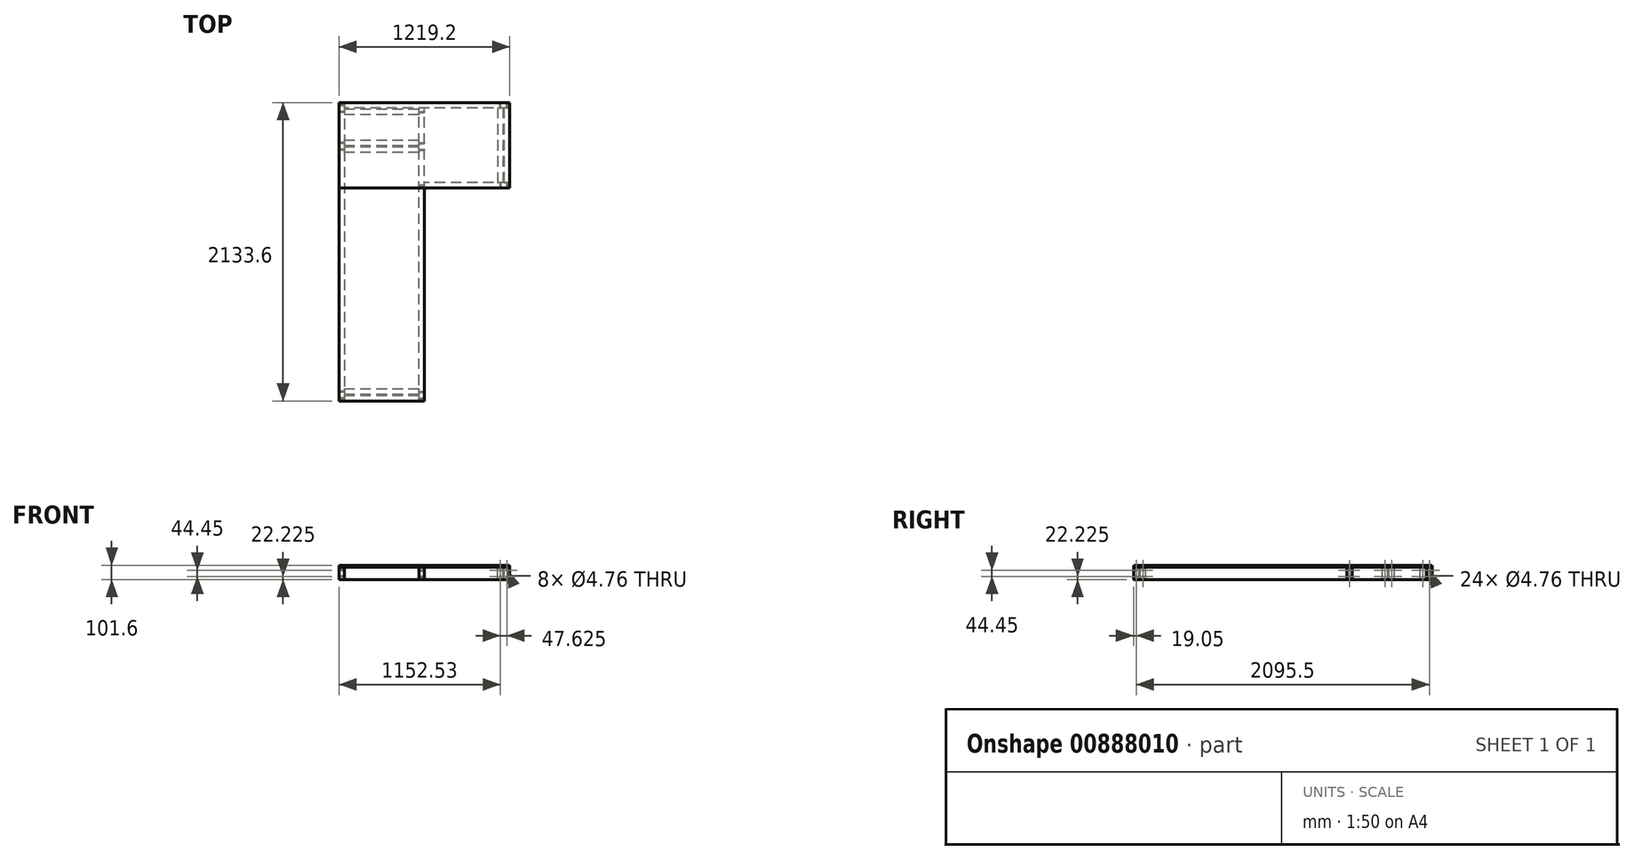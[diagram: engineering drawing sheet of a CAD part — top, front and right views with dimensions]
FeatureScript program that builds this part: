
annotation { "Feature Type Name" : "Feature", "Feature Type Description" : "" }
export const myFeature = defineFeature(function(context is Context, id is Id, definition is map)
    precondition{}
    {
        {
            var Q0;
            Q0=qCreatedBy(makeId("Top.planeOp"),FACE);
            var sketch = newSketch(context, id + "F0", { "sketchPlane" : qUnion([Q0])});
            skLineSegment(sketch, "E0.bottom", {"start": v(0, 0) * mm, "end": v(1219.2, 0) * mm});
            skLineSegment(sketch, "E0.top", {"start": v(0, 609.6) * mm, "end": v(1219.2, 609.6) * mm});
            skLineSegment(sketch, "E0.left", {"start": v(0, 0) * mm, "end": v(0, 609.6) * mm});
            skLineSegment(sketch, "E0.right", {"start": v(1219.2, 0) * mm, "end": v(1219.2, 609.6) * mm});
            skLineSegment(sketch, "E1.bottom", {"start": v(0, 0) * mm, "end": v(609.6, 0) * mm});
            skSolve(sketch);
        }
        {
            var Q0;
            Q0 = qSketchRegion(id + "F0", true);
            extrude(context, id + "F1", {"entities" : qUnion([Q0]), "depth" : 12.7 * mm, "offsetDistance" : 25.4 * mm});
        }
        {
            var Q0;
            Q0=qCreatedBy(makeId("Top.planeOp"),FACE);
            var sketch = newSketch(context, id + "F2", { "sketchPlane" : qUnion([Q0])});
            skLineSegment(sketch, "E2.bottom", {"start": v(0, 0) * mm, "end": v(609.6, 0) * mm});
            skLineSegment(sketch, "E2.top", {"start": v(0, -1524) * mm, "end": v(609.6, -1524) * mm});
            skLineSegment(sketch, "E2.left", {"start": v(0, 0) * mm, "end": v(0, -1524) * mm});
            skLineSegment(sketch, "E2.right", {"start": v(609.6, 0) * mm, "end": v(609.6, -1524) * mm});
            skSolve(sketch);
        }
        {
            var Q0;
            Q0 = qSketchRegion(id + "F2", true);
            extrude(context, id + "F3", {"entities" : qUnion([Q0]), "depth" : 12.7 * mm, "offsetDistance" : 25.4 * mm});
        }
        {
            var Q0;
            Q0=qCreatedBy(makeId("Top.planeOp"),FACE);
            var sketch = newSketch(context, id + "F4", { "sketchPlane" : qUnion([Q0])});
            skLineSegment(sketch, "E3.bottom", {"start": v(38.1, 609.6) * mm, "end": v(0, 609.6) * mm});
            skLineSegment(sketch, "E3.top", {"start": v(38.1, -1524) * mm, "end": v(0, -1524) * mm});
            skLineSegment(sketch, "E3.left", {"start": v(38.1, 609.6) * mm, "end": v(38.1, -1524) * mm});
            skLineSegment(sketch, "E3.right", {"start": v(0, 609.6) * mm, "end": v(0, -1524) * mm});
            skPoint(sketch, "E4", {"position": v(0, 0) * mm});
            skLineSegment(sketch, "E5.bottom", {"start": v(609.6, -1524) * mm, "end": v(571.5, -1524) * mm});
            skLineSegment(sketch, "E5.top", {"start": v(609.6, 571.5) * mm, "end": v(571.5, 571.5) * mm});
            skLineSegment(sketch, "E5.left", {"start": v(609.6, -1524) * mm, "end": v(609.6, 571.5) * mm});
            skLineSegment(sketch, "E5.right", {"start": v(571.5, -1524) * mm, "end": v(571.5, 571.5) * mm});
            skLineSegment(sketch, "E6.bottom", {"start": v(1219.2, 609.6) * mm, "end": v(38.1, 609.6) * mm});
            skLineSegment(sketch, "E6.top", {"start": v(1219.2, 571.5) * mm, "end": v(38.1, 571.5) * mm});
            skLineSegment(sketch, "E6.left", {"start": v(1219.2, 609.6) * mm, "end": v(1219.2, 571.5) * mm});
            skLineSegment(sketch, "E6.right", {"start": v(38.1, 609.6) * mm, "end": v(38.1, 571.5) * mm});
            skLineSegment(sketch, "E7.bottom", {"start": v(1219.2, 0) * mm, "end": v(609.6, 0) * mm});
            skLineSegment(sketch, "E7.top", {"start": v(1219.2, 38.1) * mm, "end": v(609.6, 38.1) * mm});
            skLineSegment(sketch, "E7.left", {"start": v(1219.2, 0) * mm, "end": v(1219.2, 38.1) * mm});
            skLineSegment(sketch, "E7.right", {"start": v(609.6, 0) * mm, "end": v(609.6, 38.1) * mm});
            skLineSegment(sketch, "E8.bottom", {"start": v(1219.2, 38.1) * mm, "end": v(1181.1, 38.1) * mm});
            skLineSegment(sketch, "E8.top", {"start": v(1219.2, 571.5) * mm, "end": v(1181.1, 571.5) * mm});
            skLineSegment(sketch, "E8.left", {"start": v(1219.2, 38.1) * mm, "end": v(1219.2, 571.5) * mm});
            skLineSegment(sketch, "E8.right", {"start": v(1181.1, 38.1) * mm, "end": v(1181.1, 571.5) * mm});
            skLineSegment(sketch, "E9.bottom", {"start": v(571.5, -1524) * mm, "end": v(38.1, -1524) * mm});
            skLineSegment(sketch, "E9.top", {"start": v(571.5, -1485.9) * mm, "end": v(38.1, -1485.9) * mm});
            skLineSegment(sketch, "E9.left", {"start": v(571.5, -1524) * mm, "end": v(571.5, -1485.9) * mm});
            skLineSegment(sketch, "E9.right", {"start": v(38.1, -1524) * mm, "end": v(38.1, -1485.9) * mm});
            skLineSegment(sketch, "E10.bottom", {"start": v(571.5, 254) * mm, "end": v(38.1, 254) * mm});
            skLineSegment(sketch, "E10.top", {"start": v(571.5, 292.1) * mm, "end": v(38.1, 292.1) * mm});
            skLineSegment(sketch, "E10.left", {"start": v(571.5, 254) * mm, "end": v(571.5, 292.1) * mm});
            skLineSegment(sketch, "E10.right", {"start": v(38.1, 254) * mm, "end": v(38.1, 292.1) * mm});
            skLineSegment(sketch, "E11.bottom", {"start": v(571.5, 301.63) * mm, "end": v(38.1, 301.63) * mm});
            skLineSegment(sketch, "E11.top", {"start": v(571.5, 339.73) * mm, "end": v(38.1, 339.73) * mm});
            skLineSegment(sketch, "E11.left", {"start": v(571.5, 301.63) * mm, "end": v(571.5, 339.72) * mm});
            skLineSegment(sketch, "E11.right", {"start": v(38.1, 301.62) * mm, "end": v(38.1, 339.73) * mm});
            skLineSegment(sketch, "E12.bottom", {"start": v(571.5, -1476.38) * mm, "end": v(38.1, -1476.38) * mm});
            skLineSegment(sketch, "E12.top", {"start": v(571.5, -1438.28) * mm, "end": v(38.1, -1438.28) * mm});
            skLineSegment(sketch, "E12.left", {"start": v(571.5, -1476.38) * mm, "end": v(571.5, -1438.28) * mm});
            skLineSegment(sketch, "E12.right", {"start": v(38.1, -1476.38) * mm, "end": v(38.1, -1438.28) * mm});
            skLineSegment(sketch, "E13.bottom", {"start": v(571.5, 561.98) * mm, "end": v(38.1, 561.98) * mm});
            skLineSegment(sketch, "E13.top", {"start": v(571.5, 523.88) * mm, "end": v(38.1, 523.88) * mm});
            skLineSegment(sketch, "E13.left", {"start": v(571.5, 561.98) * mm, "end": v(571.5, 523.88) * mm});
            skLineSegment(sketch, "E13.right", {"start": v(38.1, 561.98) * mm, "end": v(38.1, 523.88) * mm});
            skLineSegment(sketch, "E14.bottom", {"start": v(1171.58, 571.5) * mm, "end": v(1133.47, 571.5) * mm});
            skLineSegment(sketch, "E14.top", {"start": v(1171.58, 38.1) * mm, "end": v(1133.48, 38.1) * mm});
            skLineSegment(sketch, "E14.left", {"start": v(1171.58, 571.5) * mm, "end": v(1171.58, 38.1) * mm});
            skLineSegment(sketch, "E14.right", {"start": v(1133.47, 571.5) * mm, "end": v(1133.47, 38.1) * mm});
            skLineSegment(sketch, "E15", {"start": v(38.1, 320.68) * mm, "end": v(571.5, 320.68) * mm, "construction": true});
            skLineSegment(sketch, "E16", {"start": v(38.1, 273.05) * mm, "end": v(571.5, 273.05) * mm, "construction": true});
            skLineSegment(sketch, "E17", {"start": v(38.1, 542.93) * mm, "end": v(571.5, 542.93) * mm, "construction": true});
            skLineSegment(sketch, "E18", {"start": v(38.1, 590.55) * mm, "end": v(1219.2, 590.55) * mm, "construction": true});
            skLineSegment(sketch, "E19", {"start": v(1152.53, 571.5) * mm, "end": v(1152.53, 38.1) * mm, "construction": true});
            skLineSegment(sketch, "E20", {"start": v(1200.15, 38.1) * mm, "end": v(1200.15, 571.5) * mm, "construction": true});
            skLineSegment(sketch, "E21", {"start": v(38.1, -1457.33) * mm, "end": v(571.5, -1457.33) * mm, "construction": true});
            skLineSegment(sketch, "E22", {"start": v(38.1, -1504.95) * mm, "end": v(571.5, -1504.95) * mm, "construction": true});
            skSolve(sketch);
        }
        {
            var Q0;
            {var subQ1=sQuery(id+"F4.wireOp",EDGE,"E3.bottom");Q0=makeQuery(id+"F4.imprint","IMPRINT",FACE,{"disambiguationData":[TD([[makeQuery(id+"F4.imprint","IMPRINT",EDGE,{"derivedFrom":subQ1}),1.0]])]});}
            extrude(context, id + "F5", {"entities" : qUnion([Q0]), "oppositeDirection" : true, "depth" : 88.9 * mm, "offsetDistance" : 25.4 * mm});
        }
        {
            var Q0;
            {var subQ0=sQuery(id+"F4.wireOp",EDGE,"E9.bottom");Q0=makeQuery(id+"F4.imprint","IMPRINT",FACE,{"disambiguationData":[TD([[makeQuery(id+"F4.imprint","IMPRINT",EDGE,{"derivedFrom":subQ0}),-1.0]])]});}
            extrude(context, id + "F6", {"entities" : qUnion([Q0]), "oppositeDirection" : true, "depth" : 88.9 * mm, "offsetDistance" : 25.4 * mm});
        }
        {
            var Q0;
            {var subQ5=sQuery(id+"F4.wireOp",EDGE,"E5.bottom");Q0=makeQuery(id+"F4.imprint","IMPRINT",FACE,{"disambiguationData":[TD([[makeQuery(id+"F4.imprint","IMPRINT",EDGE,{"derivedFrom":subQ5}),-1.0]])]});}
            extrude(context, id + "F7", {"entities" : qUnion([Q0]), "oppositeDirection" : true, "depth" : 88.9 * mm, "offsetDistance" : 25.4 * mm});
        }
        {
            var Q0;
            {var subQ4=sQuery(id+"F4.wireOp",EDGE,"E7.bottom");Q0=makeQuery(id+"F4.imprint","IMPRINT",FACE,{"disambiguationData":[TD([[makeQuery(id+"F4.imprint","IMPRINT",EDGE,{"derivedFrom":subQ4}),-1.0]])]});}
            extrude(context, id + "F8", {"entities" : qUnion([Q0]), "oppositeDirection" : true, "depth" : 88.9 * mm, "offsetDistance" : 25.4 * mm});
        }
        {
            var Q0;
            {var subQ0=sQuery(id+"F4.wireOp",EDGE,"E10.bottom");Q0=makeQuery(id+"F4.imprint","IMPRINT",FACE,{"disambiguationData":[TD([[makeQuery(id+"F4.imprint","IMPRINT",EDGE,{"derivedFrom":subQ0}),-1.0]])]});}
            extrude(context, id + "F9", {"entities" : qUnion([Q0]), "oppositeDirection" : true, "depth" : 88.9 * mm, "offsetDistance" : 25.4 * mm});
        }
        {
            var Q0;
            {var subQ1=sQuery(id+"F4.wireOp",EDGE,"E5.top");Q0=makeQuery(id+"F4.imprint","IMPRINT",FACE,{"disambiguationData":[TD([[makeQuery(id+"F4.imprint","IMPRINT",EDGE,{"derivedFrom":subQ1}),-1.0]])]});}
            extrude(context, id + "F10", {"entities" : qUnion([Q0]), "oppositeDirection" : true, "depth" : 88.9 * mm, "offsetDistance" : 25.4 * mm});
        }
        {
            var Q0;
            {var subQ0=sQuery(id+"F4.wireOp",EDGE,"E8.left");Q0=makeQuery(id+"F4.imprint","IMPRINT",FACE,{"disambiguationData":[TD([[makeQuery(id+"F4.imprint","IMPRINT",EDGE,{"derivedFrom":subQ0}),1.0]])]});}
            extrude(context, id + "F11", {"entities" : qUnion([Q0]), "oppositeDirection" : true, "depth" : 88.9 * mm, "offsetDistance" : 25.4 * mm});
        }
        {
            var Q0;
            {var subQ0=sQuery(id+"F4.wireOp",EDGE,"E11.bottom");Q0=makeQuery(id+"F4.imprint","IMPRINT",FACE,{"disambiguationData":[TD([[makeQuery(id+"F4.imprint","IMPRINT",EDGE,{"derivedFrom":subQ0}),-1.0]])]});}
            extrude(context, id + "F12", {"entities" : qUnion([Q0]), "oppositeDirection" : true, "depth" : 88.9 * mm, "offsetDistance" : 25.4 * mm});
        }
        {
            var Q0;
            {var subQ0=sQuery(id+"F4.wireOp",EDGE,"E12.bottom");Q0=makeQuery(id+"F4.imprint","IMPRINT",FACE,{"disambiguationData":[TD([[makeQuery(id+"F4.imprint","IMPRINT",EDGE,{"derivedFrom":subQ0}),-1.0]])]});}
            extrude(context, id + "F13", {"entities" : qUnion([Q0]), "oppositeDirection" : true, "depth" : 88.9 * mm, "offsetDistance" : 25.4 * mm});
        }
        {
            var Q0;
            {var subQ0=sQuery(id+"F4.wireOp",EDGE,"E13.bottom");Q0=makeQuery(id+"F4.imprint","IMPRINT",FACE,{"disambiguationData":[TD([[makeQuery(id+"F4.imprint","IMPRINT",EDGE,{"derivedFrom":subQ0}),1.0]])]});}
            extrude(context, id + "F14", {"entities" : qUnion([Q0]), "oppositeDirection" : true, "depth" : 88.9 * mm, "offsetDistance" : 25.4 * mm});
        }
        {
            var Q0;
            {var subQ0=sQuery(id+"F4.wireOp",EDGE,"E14.left");Q0=makeQuery(id+"F4.imprint","IMPRINT",FACE,{"disambiguationData":[TD([[makeQuery(id+"F4.imprint","IMPRINT",EDGE,{"derivedFrom":subQ0}),-1.0]])]});}
            extrude(context, id + "F15", {"entities" : qUnion([Q0]), "oppositeDirection" : true, "depth" : 88.9 * mm, "offsetDistance" : 25.4 * mm});
        }
        {
            var Q0;
            Q0=makeQuery(id+"F5.opExtrude","CAP_EDGE",EDGE,{"disambiguationData":[OSD([sQuery(id+"F4.wireOp",EDGE,"E3.right")])],"isStart":false});
            var Q1;
            Q1=makeQuery(id+"F5.opExtrude","CAP_EDGE",EDGE,{"disambiguationData":[OSD([sQuery(id+"F4.wireOp",EDGE,"E3.left")])],"isStart":false});
            var Q2;
            Q2=makeQuery(id+"F7.opExtrude","CAP_EDGE",EDGE,{"disambiguationData":[OSD([sQuery(id+"F4.wireOp",EDGE,"E5.right")])],"isStart":false});
            var Q3;
            Q3=makeQuery(id+"F7.opExtrude","CAP_EDGE",EDGE,{"disambiguationData":[OSD([sQuery(id+"F4.wireOp",EDGE,"E5.left")])],"isStart":false});
            var Q4;
            Q4=makeQuery(id+"F7.opExtrude","CAP_EDGE",EDGE,{"disambiguationData":[OSD([sQuery(id+"F4.wireOp",EDGE,"E5.right")])],"isStart":true});
            var Q5;
            Q5=makeQuery(id+"F5.opExtrude","CAP_EDGE",EDGE,{"disambiguationData":[OSD([sQuery(id+"F4.wireOp",EDGE,"E3.left")])],"isStart":true});
            var Q6;
            Q6=makeQuery(id+"F5.opExtrude","CAP_EDGE",EDGE,{"disambiguationData":[OSD([sQuery(id+"F4.wireOp",EDGE,"E3.right")])],"isStart":true});
            var Q7;
            Q7=makeQuery(id+"F6.opExtrude","CAP_EDGE",EDGE,{"disambiguationData":[OSD([sQuery(id+"F4.wireOp",EDGE,"E9.top")])],"isStart":true});
            var Q8;
            Q8=makeQuery(id+"F6.opExtrude","CAP_EDGE",EDGE,{"disambiguationData":[OSD([sQuery(id+"F4.wireOp",EDGE,"E9.bottom")])],"isStart":true});
            var Q9;
            Q9=makeQuery(id+"F7.opExtrude","CAP_EDGE",EDGE,{"disambiguationData":[OSD([sQuery(id+"F4.wireOp",EDGE,"E5.left")])],"isStart":true});
            var Q10;
            Q10=makeQuery(id+"F6.opExtrude","CAP_EDGE",EDGE,{"disambiguationData":[OSD([sQuery(id+"F4.wireOp",EDGE,"E9.top")])],"isStart":false});
            var Q11;
            Q11=makeQuery(id+"F6.opExtrude","CAP_EDGE",EDGE,{"disambiguationData":[OSD([sQuery(id+"F4.wireOp",EDGE,"E9.bottom")])],"isStart":false});
            var Q12;
            Q12=makeQuery(id+"F9.opExtrude","CAP_EDGE",EDGE,{"disambiguationData":[OSD([sQuery(id+"F4.wireOp",EDGE,"E10.bottom")])],"isStart":false});
            var Q13;
            Q13=makeQuery(id+"F9.opExtrude","CAP_EDGE",EDGE,{"disambiguationData":[OSD([sQuery(id+"F4.wireOp",EDGE,"E10.top")])],"isStart":true});
            var Q14;
            Q14=makeQuery(id+"F9.opExtrude","CAP_EDGE",EDGE,{"disambiguationData":[OSD([sQuery(id+"F4.wireOp",EDGE,"E10.top")])],"isStart":false});
            var Q15;
            Q15=makeQuery(id+"F8.opExtrude","CAP_EDGE",EDGE,{"disambiguationData":[OSD([sQuery(id+"F4.wireOp",EDGE,"E7.top")])],"isStart":false});
            var Q16;
            Q16=makeQuery(id+"F8.opExtrude","CAP_EDGE",EDGE,{"disambiguationData":[OSD([sQuery(id+"F4.wireOp",EDGE,"E7.bottom")])],"isStart":false});
            var Q17;
            Q17=makeQuery(id+"F11.opExtrude","CAP_EDGE",EDGE,{"disambiguationData":[OSD([sQuery(id+"F4.wireOp",EDGE,"E8.left")])],"isStart":false});
            var Q18;
            Q18=makeQuery(id+"F8.opExtrude","CAP_EDGE",EDGE,{"disambiguationData":[OSD([sQuery(id+"F4.wireOp",EDGE,"E7.top")])],"isStart":true});
            var Q19;
            Q19=makeQuery(id+"F11.opExtrude","CAP_EDGE",EDGE,{"disambiguationData":[OSD([sQuery(id+"F4.wireOp",EDGE,"E8.right")])],"isStart":false});
            var Q20;
            Q20=makeQuery(id+"F10.opExtrude","CAP_EDGE",EDGE,{"disambiguationData":[OSD([sQuery(id+"F4.wireOp",EDGE,"E5.top"),sQuery(id+"F4.wireOp",EDGE,"E6.top")])],"isStart":false});
            var Q21;
            Q21=makeQuery(id+"F10.opExtrude","CAP_EDGE",EDGE,{"disambiguationData":[OSD([sQuery(id+"F4.wireOp",EDGE,"E6.bottom")])],"isStart":false});
            var Q22;
            Q22=makeQuery(id+"F10.opExtrude","CAP_EDGE",EDGE,{"disambiguationData":[OSD([sQuery(id+"F4.wireOp",EDGE,"E6.bottom")])],"isStart":true});
            var Q23;
            Q23=makeQuery(id+"F9.opExtrude","CAP_EDGE",EDGE,{"disambiguationData":[OSD([sQuery(id+"F4.wireOp",EDGE,"E10.bottom")])],"isStart":true});
            var Q24;
            Q24=makeQuery(id+"F8.opExtrude","CAP_EDGE",EDGE,{"disambiguationData":[OSD([sQuery(id+"F4.wireOp",EDGE,"E7.bottom")])],"isStart":true});
            var Q25;
            Q25=makeQuery(id+"F11.opExtrude","CAP_EDGE",EDGE,{"disambiguationData":[OSD([sQuery(id+"F4.wireOp",EDGE,"E8.right")])],"isStart":true});
            var Q26;
            Q26=makeQuery(id+"F11.opExtrude","CAP_EDGE",EDGE,{"disambiguationData":[OSD([sQuery(id+"F4.wireOp",EDGE,"E8.left")])],"isStart":true});
            var Q27;
            Q27=makeQuery(id+"F10.opExtrude","CAP_EDGE",EDGE,{"disambiguationData":[OSD([sQuery(id+"F4.wireOp",EDGE,"E5.top"),sQuery(id+"F4.wireOp",EDGE,"E6.top")])],"isStart":true});
            var Q28;
            Q28=makeQuery(id+"F12.opExtrude","CAP_EDGE",EDGE,{"disambiguationData":[OSD([sQuery(id+"F4.wireOp",EDGE,"E11.top")])],"isStart":false});
            var Q29;
            Q29=makeQuery(id+"F12.opExtrude","CAP_EDGE",EDGE,{"disambiguationData":[OSD([sQuery(id+"F4.wireOp",EDGE,"E11.bottom")])],"isStart":false});
            var Q30;
            Q30=makeQuery(id+"F12.opExtrude","CAP_EDGE",EDGE,{"disambiguationData":[OSD([sQuery(id+"F4.wireOp",EDGE,"E11.top")])],"isStart":true});
            var Q31;
            Q31=makeQuery(id+"F9.opExtrude","CAP_EDGE",EDGE,{"disambiguationData":[OSD([sQuery(id+"F4.wireOp",EDGE,"E11.bottom")])],"isStart":true});
            var Q32;
            Q32=makeQuery(id+"F9.opExtrude","CAP_EDGE",EDGE,{"disambiguationData":[OSD([sQuery(id+"F4.wireOp",EDGE,"E11.bottom")])],"isStart":false});
            var Q33;
            Q33=makeQuery(id+"F14.opExtrude","CAP_EDGE",EDGE,{"disambiguationData":[OSD([sQuery(id+"F4.wireOp",EDGE,"E13.top")])],"isStart":false});
            var Q34;
            Q34=makeQuery(id+"F14.opExtrude","CAP_EDGE",EDGE,{"disambiguationData":[OSD([sQuery(id+"F4.wireOp",EDGE,"E13.bottom")])],"isStart":false});
            var Q35;
            Q35=makeQuery(id+"F14.opExtrude","CAP_EDGE",EDGE,{"disambiguationData":[OSD([sQuery(id+"F4.wireOp",EDGE,"E13.top")])],"isStart":true});
            var Q36;
            Q36=makeQuery(id+"F14.opExtrude","CAP_EDGE",EDGE,{"disambiguationData":[OSD([sQuery(id+"F4.wireOp",EDGE,"E13.bottom")])],"isStart":true});
            var Q37;
            Q37=makeQuery(id+"F13.opExtrude","CAP_EDGE",EDGE,{"disambiguationData":[OSD([sQuery(id+"F4.wireOp",EDGE,"E12.top")])],"isStart":false});
            var Q38;
            Q38=makeQuery(id+"F13.opExtrude","CAP_EDGE",EDGE,{"disambiguationData":[OSD([sQuery(id+"F4.wireOp",EDGE,"E12.bottom")])],"isStart":false});
            var Q39;
            Q39=makeQuery(id+"F13.opExtrude","CAP_EDGE",EDGE,{"disambiguationData":[OSD([sQuery(id+"F4.wireOp",EDGE,"E12.bottom")])],"isStart":true});
            var Q40;
            Q40=makeQuery(id+"F13.opExtrude","CAP_EDGE",EDGE,{"disambiguationData":[OSD([sQuery(id+"F4.wireOp",EDGE,"E12.top")])],"isStart":true});
            var Q41;
            Q41=makeQuery(id+"F15.opExtrude","CAP_EDGE",EDGE,{"disambiguationData":[OSD([sQuery(id+"F4.wireOp",EDGE,"E14.right")])],"isStart":false});
            var Q42;
            Q42=makeQuery(id+"F15.opExtrude","CAP_EDGE",EDGE,{"disambiguationData":[OSD([sQuery(id+"F4.wireOp",EDGE,"E14.left")])],"isStart":false});
            var Q43;
            Q43=makeQuery(id+"F15.opExtrude","CAP_EDGE",EDGE,{"disambiguationData":[OSD([sQuery(id+"F4.wireOp",EDGE,"E14.left")])],"isStart":true});
            var Q44;
            Q44=makeQuery(id+"F15.opExtrude","CAP_EDGE",EDGE,{"disambiguationData":[OSD([sQuery(id+"F4.wireOp",EDGE,"E14.right")])],"isStart":true});
            var Q45;
            Q45=makeQuery(id+"F12.opExtrude","CAP_EDGE",EDGE,{"disambiguationData":[OSD([sQuery(id+"F4.wireOp",EDGE,"E11.bottom")])],"isStart":true});
            fillet(context, id + "F16", {"entities" : qUnion([Q0, Q1, Q2, Q3, Q4, Q5, Q6, Q7, Q8, Q9, Q10, Q11, Q12, Q13, Q14, Q15, Q16, Q17, Q18, Q19, Q20, Q21, Q22, Q23, Q24, Q25, Q26, Q27, Q28, Q29, Q30, Q31, Q32, Q33, Q34, Q35, Q36, Q37, Q38, Q39, Q40, Q41, Q42, Q43, Q44, Q45]), "radius" : 5.08 * mm, "tangentPropagation" : true, "allowEdgeOverflow" : false});
        }
        {
            var Q0;
            Q0=makeQuery(id+"F5.opExtrude","SWEPT_FACE",FACE,{"disambiguationData":[OSD([sQuery(id+"F4.wireOp",EDGE,"E3.right")])]});
            var sketch = newSketch(context, id + "F17", { "sketchPlane" : qUnion([Q0])});
            skCircle(sketch, "E23", {"center": v(-590.55, -22.23) * mm, "radius": 2.38 * mm});
            skLineSegment(sketch, "E24", {"start": v(-609.6, -44.45) * mm, "end": v(-571.5, -44.45) * mm, "construction": true});
            skLineSegment(sketch, "E25", {"start": v(-590.55, -44.45) * mm, "end": v(-590.55, 0) * mm, "construction": true});
            skLineSegment(sketch, "E26", {"start": v(-590.55, -44.45) * mm, "end": v(-590.55, -88.67) * mm, "construction": true});
            skCircle(sketch, "E27", {"center": v(-590.55, -66.56) * mm, "radius": 2.38 * mm});
            skLineSegment(sketch, "E28", {"start": v(-561.98, -44.45) * mm, "end": v(-523.88, -44.45) * mm, "construction": true});
            skCircle(sketch, "E29", {"center": v(-542.93, -66.64) * mm, "radius": 2.38 * mm});
            skCircle(sketch, "E30", {"center": v(-542.93, -22.23) * mm, "radius": 2.38 * mm});
            skLineSegment(sketch, "E31", {"start": v(-542.93, -44.45) * mm, "end": v(-542.93, 0) * mm, "construction": true});
            skLineSegment(sketch, "E32", {"start": v(-542.93, -44.45) * mm, "end": v(-542.93, -88.83) * mm, "construction": true});
            skLineSegment(sketch, "E33", {"start": v(-301.63, -44.45) * mm, "end": v(-339.73, -44.45) * mm, "construction": true});
            skLineSegment(sketch, "E34", {"start": v(-320.68, -44.45) * mm, "end": v(-320.68, 0) * mm, "construction": true});
            skLineSegment(sketch, "E35", {"start": v(-320.68, -44.45) * mm, "end": v(-320.68, -88.9) * mm, "construction": true});
            skCircle(sketch, "E36", {"center": v(-320.68, -22.22) * mm, "radius": 2.38 * mm});
            skCircle(sketch, "E37", {"center": v(-320.68, -66.67) * mm, "radius": 2.38 * mm});
            skLineSegment(sketch, "E38", {"start": v(-292.1, -44.45) * mm, "end": v(-254, -44.45) * mm, "construction": true});
            skLineSegment(sketch, "E39", {"start": v(-273.05, -44.45) * mm, "end": v(-273.05, 0) * mm, "construction": true});
            skLineSegment(sketch, "E40", {"start": v(-273.05, -44.45) * mm, "end": v(-273.05, -88.9) * mm, "construction": true});
            skCircle(sketch, "E41", {"center": v(-273.05, -22.22) * mm, "radius": 2.38 * mm});
            skCircle(sketch, "E42", {"center": v(-273.05, -66.67) * mm, "radius": 2.38 * mm});
            skLineSegment(sketch, "E43", {"start": v(1438.28, -44.45) * mm, "end": v(1476.38, -44.45) * mm, "construction": true});
            skLineSegment(sketch, "E44", {"start": v(1457.33, -44.45) * mm, "end": v(1457.33, 0) * mm, "construction": true});
            skLineSegment(sketch, "E45", {"start": v(1457.33, -44.45) * mm, "end": v(1457.33, -88.9) * mm, "construction": true});
            skLineSegment(sketch, "E46", {"start": v(1485.9, -44.45) * mm, "end": v(1524, -44.45) * mm, "construction": true});
            skLineSegment(sketch, "E47", {"start": v(1504.95, -44.45) * mm, "end": v(1504.95, 0) * mm, "construction": true});
            skLineSegment(sketch, "E48", {"start": v(1504.95, -44.45) * mm, "end": v(1504.95, -88.9) * mm, "construction": true});
            skCircle(sketch, "E49", {"center": v(1457.33, -66.67) * mm, "radius": 2.38 * mm});
            skCircle(sketch, "E50", {"center": v(1457.33, -22.22) * mm, "radius": 2.38 * mm});
            skCircle(sketch, "E51", {"center": v(1504.95, -22.22) * mm, "radius": 2.38 * mm});
            skCircle(sketch, "E52", {"center": v(1504.95, -66.67) * mm, "radius": 2.38 * mm});
            skSolve(sketch);
        }
        {
            var Q0;
            Q0=makeQuery(id+"F7.opExtrude","SWEPT_FACE",FACE,{"disambiguationData":[OSD([sQuery(id+"F4.wireOp",EDGE,"E5.left")])]});
            var sketch = newSketch(context, id + "F18", { "sketchPlane" : qUnion([Q0])});
            skLineSegment(sketch, "E53", {"start": v(-1524, -44.45) * mm, "end": v(-1485.9, -44.45) * mm, "construction": true});
            skLineSegment(sketch, "E54", {"start": v(-1504.95, -44.45) * mm, "end": v(-1504.95, 0) * mm, "construction": true});
            skLineSegment(sketch, "E55", {"start": v(-1504.95, -44.45) * mm, "end": v(-1504.95, -88.9) * mm, "construction": true});
            skLineSegment(sketch, "E56", {"start": v(-1476.38, -44.45) * mm, "end": v(-1438.28, -44.45) * mm, "construction": true});
            skLineSegment(sketch, "E57", {"start": v(-1457.33, -44.45) * mm, "end": v(-1457.33, 0) * mm, "construction": true});
            skLineSegment(sketch, "E58", {"start": v(-1457.33, -44.45) * mm, "end": v(-1457.33, -88.9) * mm, "construction": true});
            skCircle(sketch, "E59", {"center": v(-1457.33, -22.22) * mm, "radius": 2.38 * mm});
            skCircle(sketch, "E60", {"center": v(-1504.95, -22.23) * mm, "radius": 2.38 * mm});
            skCircle(sketch, "E61", {"center": v(-1504.95, -66.68) * mm, "radius": 2.38 * mm});
            skCircle(sketch, "E62", {"center": v(-1457.33, -66.67) * mm, "radius": 2.38 * mm});
            skLineSegment(sketch, "E63", {"start": v(254, -44.45) * mm, "end": v(292.1, -44.45) * mm, "construction": true});
            skLineSegment(sketch, "E64", {"start": v(301.62, -44.45) * mm, "end": v(339.72, -44.45) * mm, "construction": true});
            skLineSegment(sketch, "E65", {"start": v(273.05, -44.45) * mm, "end": v(273.05, 0) * mm, "construction": true});
            skLineSegment(sketch, "E66", {"start": v(273.05, -44.45) * mm, "end": v(273.05, -88.9) * mm, "construction": true});
            skLineSegment(sketch, "E67", {"start": v(320.67, -44.45) * mm, "end": v(320.67, 0) * mm, "construction": true});
            skLineSegment(sketch, "E68", {"start": v(320.67, -44.45) * mm, "end": v(320.67, -88.9) * mm, "construction": true});
            skCircle(sketch, "E69", {"center": v(273.05, -22.22) * mm, "radius": 2.38 * mm});
            skCircle(sketch, "E70", {"center": v(273.05, -66.67) * mm, "radius": 2.38 * mm});
            skCircle(sketch, "E71", {"center": v(320.67, -22.22) * mm, "radius": 2.38 * mm});
            skCircle(sketch, "E72", {"center": v(320.67, -66.67) * mm, "radius": 2.38 * mm});
            skLineSegment(sketch, "E73", {"start": v(523.88, -44.45) * mm, "end": v(561.98, -44.45) * mm, "construction": true});
            skLineSegment(sketch, "E74", {"start": v(542.93, -44.45) * mm, "end": v(542.93, 0) * mm, "construction": true});
            skLineSegment(sketch, "E75", {"start": v(542.93, -44.45) * mm, "end": v(542.93, -88.9) * mm, "construction": true});
            skCircle(sketch, "E76", {"center": v(542.93, -22.22) * mm, "radius": 2.38 * mm});
            skCircle(sketch, "E77", {"center": v(542.93, -66.67) * mm, "radius": 2.38 * mm});
            skLineSegment(sketch, "E78", {"start": v(0, -44.45) * mm, "end": v(38.1, -44.45) * mm, "construction": true});
            skLineSegment(sketch, "E79", {"start": v(19.05, -44.45) * mm, "end": v(19.05, 0) * mm, "construction": true});
            skLineSegment(sketch, "E80", {"start": v(19.05, -44.45) * mm, "end": v(19.05, -88.9) * mm, "construction": true});
            skCircle(sketch, "E81", {"center": v(19.05, -22.22) * mm, "radius": 2.38 * mm});
            skCircle(sketch, "E82", {"center": v(19.05, -66.67) * mm, "radius": 2.38 * mm});
            skSolve(sketch);
        }
        {
            var Q0;
            Q0 = qSketchRegion(id + "F17", true);
            extrude(context, id + "F19", {"entities" : qUnion([Q0]), "operationType" : NewBodyOperationType.REMOVE, "oppositeDirection" : true, "depth" : 38.1 * mm, "offsetDistance" : 25.4 * mm});
        }
        {
            var Q0;
            Q0 = qSketchRegion(id + "F18", true);
            extrude(context, id + "F20", {"entities" : qUnion([Q0]), "operationType" : NewBodyOperationType.REMOVE, "oppositeDirection" : true, "depth" : 38.1 * mm, "offsetDistance" : 25.4 * mm});
        }
        {
            var Q0;
            Q0=makeQuery(id+"F8.opExtrude","SWEPT_FACE",FACE,{"disambiguationData":[OSD([sQuery(id+"F4.wireOp",EDGE,"E7.bottom")])]});
            var sketch = newSketch(context, id + "F21", { "sketchPlane" : qUnion([Q0])});
            skLineSegment(sketch, "E83", {"start": v(1133.48, -44.45) * mm, "end": v(1171.58, -44.45) * mm, "construction": true});
            skLineSegment(sketch, "E84", {"start": v(1152.53, -44.45) * mm, "end": v(1152.53, 0) * mm, "construction": true});
            skLineSegment(sketch, "E85", {"start": v(1152.53, -44.45) * mm, "end": v(1152.53, -88.9) * mm, "construction": true});
            skLineSegment(sketch, "E86", {"start": v(1181.1, -44.45) * mm, "end": v(1219.2, -44.45) * mm, "construction": true});
            skLineSegment(sketch, "E87", {"start": v(1200.15, -44.45) * mm, "end": v(1200.15, 0) * mm, "construction": true});
            skLineSegment(sketch, "E88", {"start": v(1200.15, -44.45) * mm, "end": v(1200.15, -88.9) * mm, "construction": true});
            skCircle(sketch, "E89", {"center": v(1200.15, -66.67) * mm, "radius": 2.38 * mm});
            skCircle(sketch, "E90", {"center": v(1200.15, -22.22) * mm, "radius": 2.38 * mm});
            skCircle(sketch, "E91", {"center": v(1152.53, -22.23) * mm, "radius": 2.38 * mm});
            skCircle(sketch, "E92", {"center": v(1152.53, -66.68) * mm, "radius": 2.38 * mm});
            skSolve(sketch);
        }
        {
            var Q0;
            Q0 = qSketchRegion(id + "F21", true);
            extrude(context, id + "F22", {"entities" : qUnion([Q0]), "operationType" : NewBodyOperationType.REMOVE, "oppositeDirection" : true, "depth" : 38.1 * mm, "offsetDistance" : 25.4 * mm});
        }
        {
            var Q0;
            Q0=makeQuery(id+"F10.opExtrude","SWEPT_FACE",FACE,{"disambiguationData":[OSD([sQuery(id+"F4.wireOp",EDGE,"E6.bottom")])]});
            var sketch = newSketch(context, id + "F23", { "sketchPlane" : qUnion([Q0])});
            skLineSegment(sketch, "E93", {"start": v(-1219.2, -44.45) * mm, "end": v(-1181.1, -44.45) * mm, "construction": true});
            skLineSegment(sketch, "E94", {"start": v(-1171.58, -44.45) * mm, "end": v(-1133.47, -44.45) * mm, "construction": true});
            skLineSegment(sketch, "E95", {"start": v(-1152.53, -44.45) * mm, "end": v(-1152.53, 0) * mm, "construction": true});
            skLineSegment(sketch, "E96", {"start": v(-1152.53, -44.45) * mm, "end": v(-1152.53, -88.9) * mm, "construction": true});
            skLineSegment(sketch, "E97", {"start": v(-1200.15, -44.45) * mm, "end": v(-1200.15, 0) * mm, "construction": true});
            skLineSegment(sketch, "E98", {"start": v(-1200.15, -44.45) * mm, "end": v(-1200.15, -88.9) * mm, "construction": true});
            skCircle(sketch, "E99", {"center": v(-1200.15, -22.23) * mm, "radius": 2.38 * mm});
            skCircle(sketch, "E100", {"center": v(-1200.15, -66.68) * mm, "radius": 2.38 * mm});
            skCircle(sketch, "E101", {"center": v(-1152.53, -22.23) * mm, "radius": 2.38 * mm});
            skCircle(sketch, "E102", {"center": v(-1152.53, -66.68) * mm, "radius": 2.38 * mm});
            skSolve(sketch);
        }
        {
            var Q0;
            Q0 = qSketchRegion(id + "F23", true);
            extrude(context, id + "F24", {"entities" : qUnion([Q0]), "operationType" : NewBodyOperationType.REMOVE, "oppositeDirection" : true, "depth" : 38.1 * mm, "offsetDistance" : 25.4 * mm});
        }
    });
